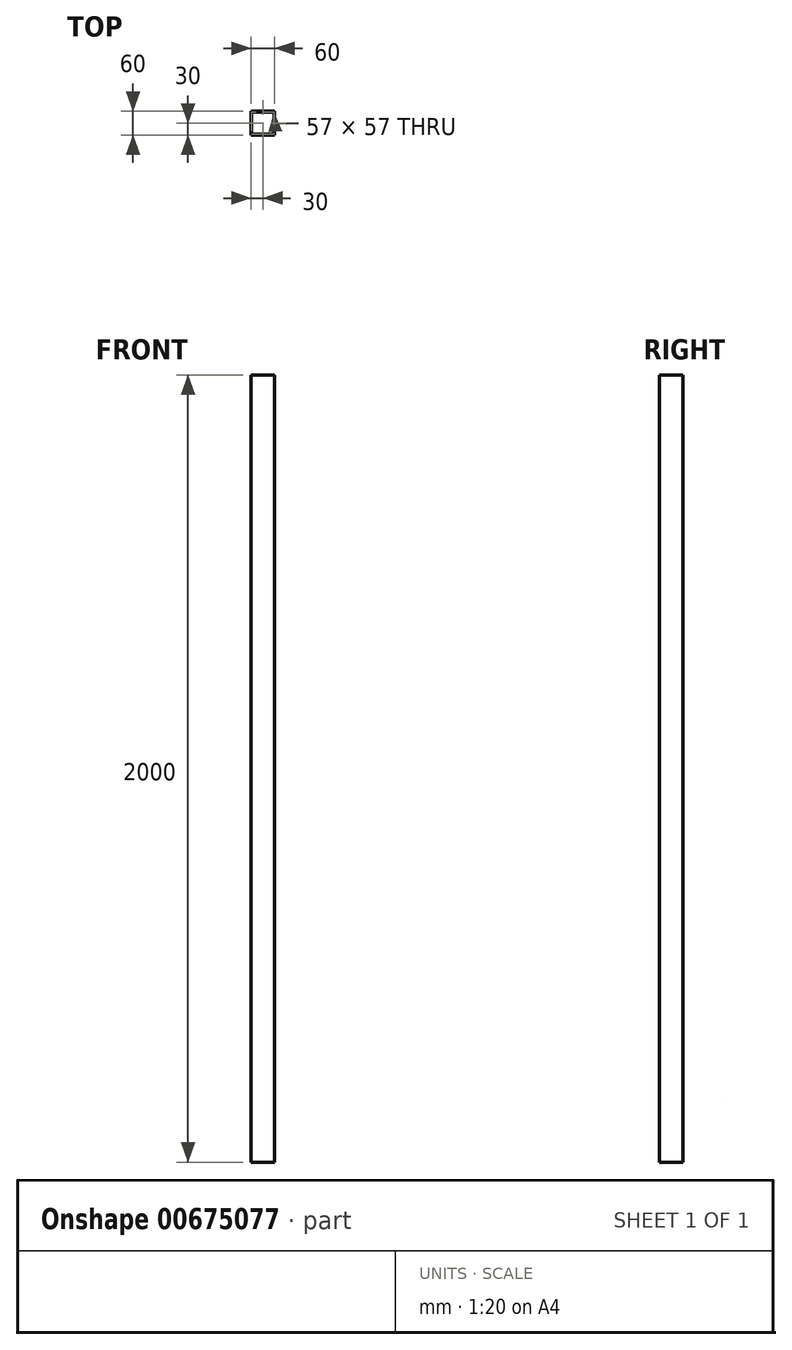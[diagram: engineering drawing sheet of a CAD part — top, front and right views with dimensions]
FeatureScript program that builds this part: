
annotation { "Feature Type Name" : "Feature", "Feature Type Description" : "" }
export const myFeature = defineFeature(function(context is Context, id is Id, definition is map)
    precondition{}
    {
        {
            var Q0;
            Q0=qCreatedBy(makeId("Top.planeOp"),FACE);
            var sketch = newSketch(context, id + "F0", { "sketchPlane" : qUnion([Q0])});
            skLineSegment(sketch, "E0.bottom", {"start": v(30, 30) * mm, "end": v(-30, 30) * mm});
            skLineSegment(sketch, "E0.top", {"start": v(30, -30) * mm, "end": v(-30, -30) * mm});
            skLineSegment(sketch, "E0.left", {"start": v(30, 30) * mm, "end": v(30, -30) * mm});
            skLineSegment(sketch, "E0.right", {"start": v(-30, 30) * mm, "end": v(-30, -30) * mm});
            skPoint(sketch, "E0.middle", {"position": v(0, 0) * mm});
            skLineSegment(sketch, "E1.bottom", {"start": v(28.5, 28.5) * mm, "end": v(-28.5, 28.5) * mm});
            skLineSegment(sketch, "E1.top", {"start": v(28.5, -28.5) * mm, "end": v(-28.5, -28.5) * mm});
            skLineSegment(sketch, "E1.left", {"start": v(28.5, 28.5) * mm, "end": v(28.5, -28.5) * mm});
            skLineSegment(sketch, "E1.right", {"start": v(-28.5, 28.5) * mm, "end": v(-28.5, -28.5) * mm});
            skSolve(sketch);
        }
        {
            var Q0;
            Q0=makeQuery(id+"F0.imprint","IMPRINT",FACE,{"disambiguationData":[TD([[makeQuery(id+"F0.imprint","IMPRINT",EDGE,{"derivedFrom":sQuery(id+"F0.wireOp",EDGE,"E0.bottom")}),1.0]])]});
            extrude(context, id + "F1", {"entities" : qUnion([Q0]), "depth" : 2000 * mm, "offsetDistance" : 25 * mm});
        }
    });
